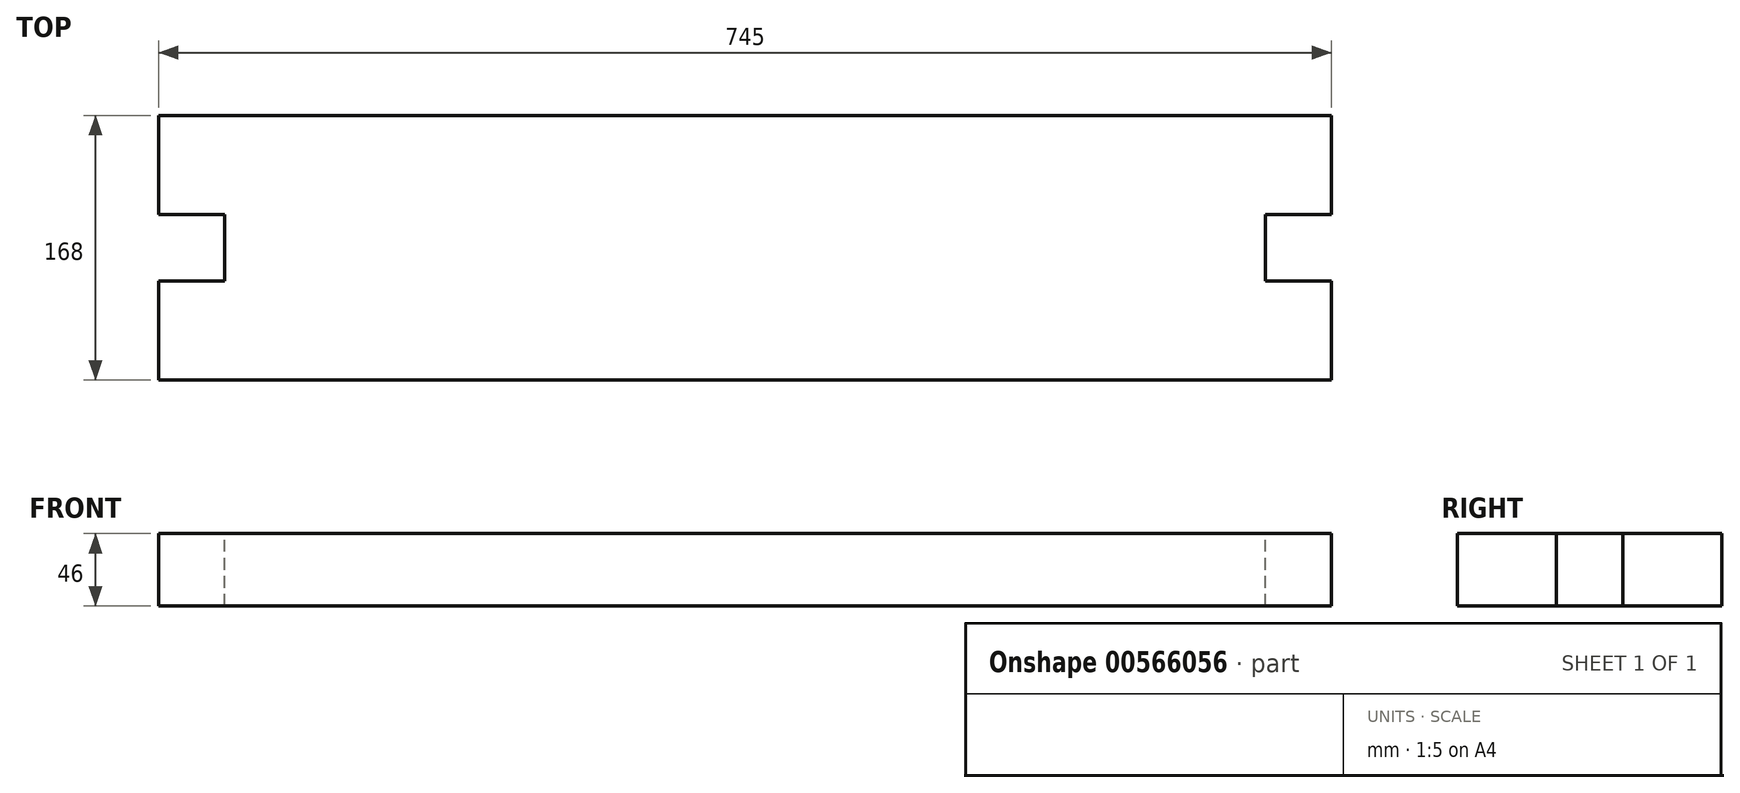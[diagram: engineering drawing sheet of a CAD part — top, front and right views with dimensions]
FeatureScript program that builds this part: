
annotation { "Feature Type Name" : "Feature", "Feature Type Description" : "" }
export const myFeature = defineFeature(function(context is Context, id is Id, definition is map)
    precondition{}
    {
        {
            var Q0;
            Q0=qCreatedBy(makeId("Top.planeOp"),FACE);
            var sketch = newSketch(context, id + "F0", { "sketchPlane" : qUnion([Q0])});
            skLineSegment(sketch, "E0.bottom", {"start": v(-173.57, 54.13) * mm, "end": v(571.43, 54.13) * mm});
            skLineSegment(sketch, "E0.top", {"start": v(-173.57, -113.87) * mm, "end": v(571.43, -113.87) * mm});
            skLineSegment(sketch, "E0.left", {"start": v(-173.57, 54.13) * mm, "end": v(-173.57, -113.87) * mm});
            skLineSegment(sketch, "E0.right", {"start": v(571.43, 54.13) * mm, "end": v(571.43, -113.87) * mm});
            skSolve(sketch);
        }
        {
            var Q0;
            Q0 = qSketchRegion(id + "F0", true);
            extrude(context, id + "F1", {"entities" : qUnion([Q0]), "depth" : 46 * mm, "offsetDistance" : 25 * mm});
        }
        {
            var Q0;
            Q0=makeQuery(id+"F1.opExtrude","CAP_FACE",FACE,{"disambiguationData":[OSD([sQuery(id+"F0.wireOp",EDGE,"E0.bottom"),sQuery(id+"F0.wireOp",EDGE,"E0.top"),sQuery(id+"F0.wireOp",EDGE,"E0.left"),sQuery(id+"F0.wireOp",EDGE,"E0.right")])],"isStart":false});
            var sketch = newSketch(context, id + "F2", { "sketchPlane" : qUnion([Q0])});
            skLineSegment(sketch, "E1", {"start": v(529.43, -29.87) * mm, "end": v(529.43, -50.86) * mm});
            skLineSegment(sketch, "E2", {"start": v(529.43, -50.86) * mm, "end": v(571.43, -50.86) * mm});
            skLineSegment(sketch, "E3", {"start": v(571.43, -50.86) * mm, "end": v(571.43, -8.86) * mm});
            skLineSegment(sketch, "E4", {"start": v(571.43, -8.86) * mm, "end": v(529.43, -8.86) * mm});
            skLineSegment(sketch, "E5", {"start": v(529.43, -8.86) * mm, "end": v(529.43, -29.87) * mm});
            skSolve(sketch);
        }
        {
            var Q0;
            Q0 = qSketchRegion(id + "F2", true);
            extrude(context, id + "F3", {"entities" : qUnion([Q0]), "operationType" : NewBodyOperationType.REMOVE, "oppositeDirection" : true, "depth" : 46 * mm, "offsetDistance" : 25 * mm});
        }
        {
            var Q0;
            Q0=makeQuery(id+"F1.opExtrude","CAP_FACE",FACE,{"disambiguationData":[OSD([sQuery(id+"F0.wireOp",EDGE,"E0.bottom"),sQuery(id+"F0.wireOp",EDGE,"E0.top"),sQuery(id+"F0.wireOp",EDGE,"E0.left"),sQuery(id+"F0.wireOp",EDGE,"E0.right")])],"isStart":false});
            var sketch = newSketch(context, id + "F4", { "sketchPlane" : qUnion([Q0])});
            skLineSegment(sketch, "E6.bottom", {"start": v(-173.57, -8.86) * mm, "end": v(-131.57, -8.86) * mm});
            skLineSegment(sketch, "E6.top", {"start": v(-173.57, -50.86) * mm, "end": v(-131.57, -50.86) * mm});
            skLineSegment(sketch, "E6.left", {"start": v(-173.57, -8.86) * mm, "end": v(-173.57, -50.86) * mm});
            skLineSegment(sketch, "E6.right", {"start": v(-131.57, -8.86) * mm, "end": v(-131.57, -50.86) * mm});
            skSolve(sketch);
        }
        {
            var Q0;
            Q0 = qSketchRegion(id + "F4", true);
            extrude(context, id + "F5", {"entities" : qUnion([Q0]), "operationType" : NewBodyOperationType.REMOVE, "oppositeDirection" : true, "depth" : 46 * mm, "offsetDistance" : 25 * mm});
        }
    });
